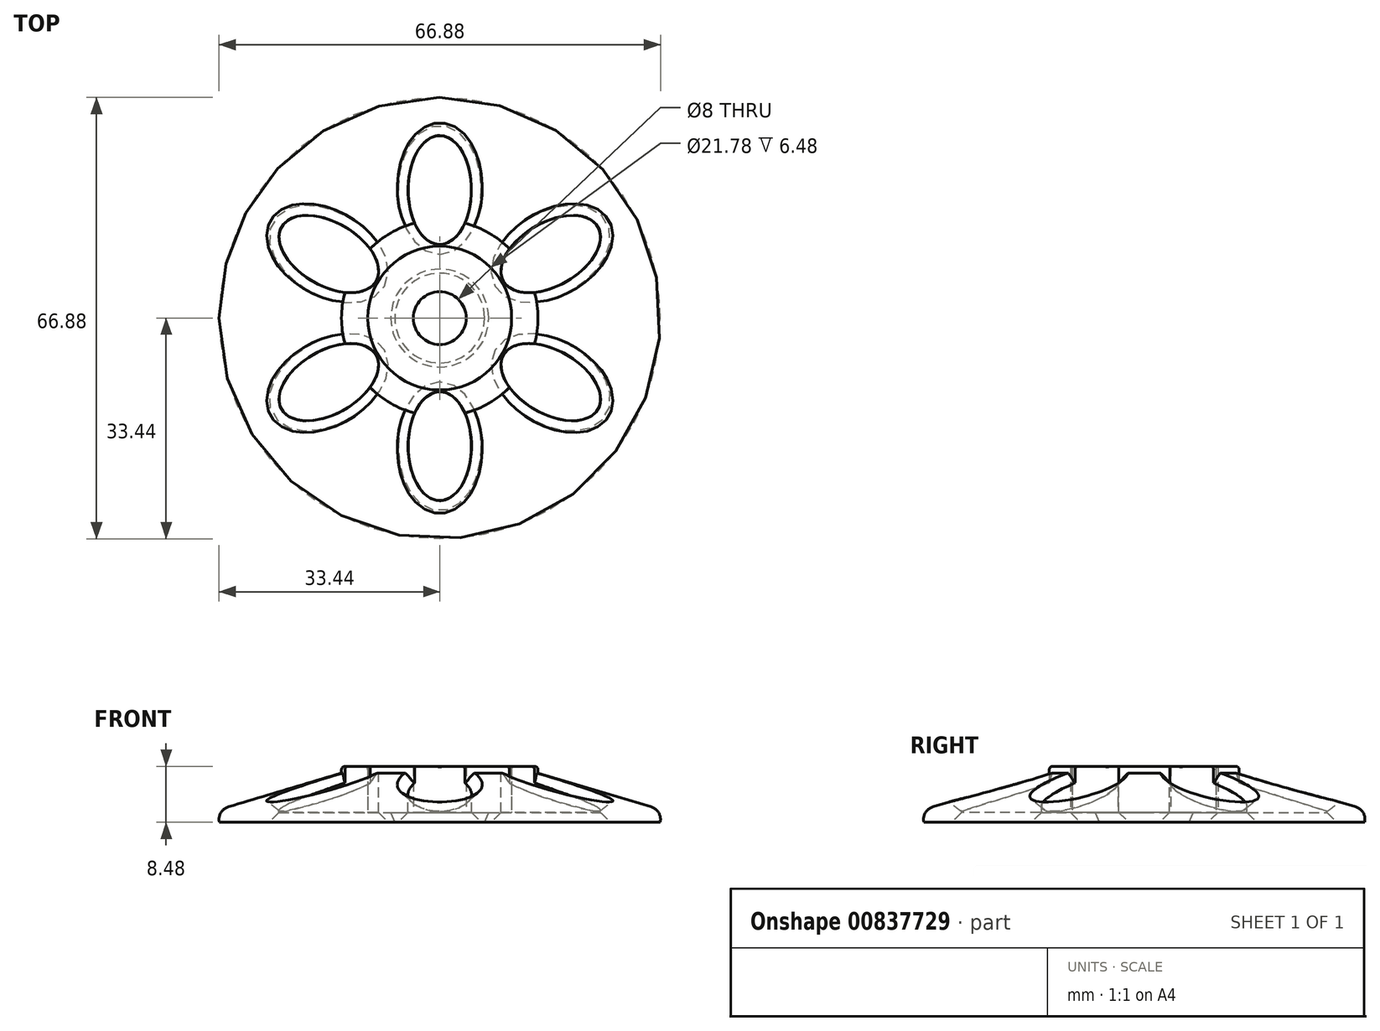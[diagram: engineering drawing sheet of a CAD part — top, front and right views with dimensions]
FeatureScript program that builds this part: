
annotation { "Feature Type Name" : "Feature", "Feature Type Description" : "" }
export const myFeature = defineFeature(function(context is Context, id is Id, definition is map)
    precondition{}
    {
        {
            var Q0;
            Q0=qCreatedBy(makeId("Front.planeOp"),FACE);
            var sketch = newSketch(context, id + "F0", { "sketchPlane" : qUnion([Q0])});
            skLineSegment(sketch, "E0", {"start": v(4, 0) * mm, "end": v(10.9, 0) * mm});
            skLineSegment(sketch, "E1", {"start": v(10.9, 0) * mm, "end": v(14.9, 0) * mm, "construction": true});
            skLineSegment(sketch, "E2.bottom", {"start": v(10.9, 0) * mm, "end": v(14.9, 0) * mm});
            skLineSegment(sketch, "E2.top", {"start": v(10.9, 6.98) * mm, "end": v(14.9, 6.98) * mm});
            skLineSegment(sketch, "E2.left", {"start": v(10.9, 0) * mm, "end": v(10.9, 6.98) * mm});
            skLineSegment(sketch, "E2.right", {"start": v(14.9, 0) * mm, "end": v(14.9, 5.98) * mm});
            skLineSegment(sketch, "E3", {"start": v(0, 0) * mm, "end": v(0, 42.81) * mm, "construction": true});
            skLineSegment(sketch, "E4", {"start": v(4, -1.5) * mm, "end": v(14.9, -1.5) * mm});
            skLineSegment(sketch, "E5", {"start": v(34.9, -1.5) * mm, "end": v(34.9, 0) * mm});
            skLineSegment(sketch, "E6", {"start": v(14.9, 0) * mm, "end": v(10.9, 0) * mm});
            skLineSegment(sketch, "E7", {"start": v(34.9, 0) * mm, "end": v(14.89, 5.98) * mm});
            skLineSegment(sketch, "E8", {"start": v(14.9, 5.98) * mm, "end": v(14.9, 6.98) * mm});
            skLineSegment(sketch, "E9", {"start": v(4, 0) * mm, "end": v(0, 0) * mm, "construction": true});
            skLineSegment(sketch, "E10", {"start": v(4, -1.5) * mm, "end": v(5, -1.5) * mm, "construction": true});
            skLineSegment(sketch, "E11", {"start": v(5, -1.5) * mm, "end": v(5, 0) * mm});
            skLineSegment(sketch, "E12.bottom", {"start": v(10.9, 0) * mm, "end": v(4, 0) * mm});
            skLineSegment(sketch, "E12.top", {"start": v(10.9, 6.98) * mm, "end": v(4, 6.98) * mm});
            skLineSegment(sketch, "E12.right", {"start": v(4, 0) * mm, "end": v(4, 6.98) * mm});
            skLineSegment(sketch, "E13", {"start": v(14.9, 0) * mm, "end": v(14.9, -1.5) * mm, "construction": true});
            skLineSegment(sketch, "E14", {"start": v(14.9, -1.5) * mm, "end": v(34.9, -1.5) * mm});
            skSolve(sketch);
        }
        {
            var Q0;
            Q0=makeQuery(id+"F0.imprint","IMPRINT",FACE,{"disambiguationData":[TD([[makeQuery(id+"F0.imprint","IMPRINT",EDGE,{"derivedFrom":sQuery(id+"F0.wireOp",EDGE,"E2.top")}),-1.0]])]});
            var Q1;
            Q1=sQuery(id+"F0.wireOp",EDGE,"E3");
            revolve(context, id + "F1", {"surfaceOperationType" : NewSurfaceOperationType.NEW, "entities" : qUnion([Q0]), "axis" : qUnion([Q1]), "revolveType" : RevolveType.FULL});
        }
        {
            var Q0;
            Q0=makeQuery(id+"F0.imprint","IMPRINT",FACE,{"disambiguationData":[TD([[makeQuery(id+"F0.imprint","IMPRINT",EDGE,{"derivedFrom":sQuery(id+"F0.wireOp",EDGE,"E12.top")}),1.0]])]});
            var Q1;
            Q1=sQuery(id+"F0.wireOp",EDGE,"E3");
            revolve(context, id + "F2", {"surfaceOperationType" : NewSurfaceOperationType.NEW, "entities" : qUnion([Q0]), "axis" : qUnion([Q1]), "revolveType" : RevolveType.FULL});
        }
        {
            var Q0;
            Q0=makeQuery(id+"F0.imprint","IMPRINT",FACE,{"disambiguationData":[TD([[makeQuery(id+"F0.imprint","IMPRINT",EDGE,{"derivedFrom":sQuery(id+"F0.wireOp",EDGE,"E2.right")}),-1.0]])]});
            var Q1;
            Q1=sQuery(id+"F0.wireOp",EDGE,"E3");
            revolve(context, id + "F3", {"surfaceOperationType" : NewSurfaceOperationType.NEW, "entities" : qUnion([Q0]), "axis" : qUnion([Q1]), "revolveType" : RevolveType.FULL});
        }
        {
            var Q0;
            Q0=qCreatedBy(makeId("Top.planeOp"),FACE);
            var sketch = newSketch(context, id + "F4", { "sketchPlane" : qUnion([Q0])});
            skPoint(sketch, "E15", {"position": v(0, 19.42) * mm});
            skEllipse(sketch, "E16", {"center": v(0, 19.42) * mm, "majorRadius": 8.25 * mm, "minorRadius": 4.8 * mm, "majorAxis": v(0, -1)});
            skSolve(sketch);
        }
        {
            var Q0;
            Q0=makeQuery(id+"F4.imprint","IMPRINT",FACE,{"disambiguationData":[TD([[makeQuery(id+"F4.imprint","IMPRINT",EDGE,{"derivedFrom":sQuery(id+"F4.wireOp",EDGE,"E16")}),1.0]])]});
            extrude(context, id + "F5", {"entities" : qUnion([Q0]), "endBound" : BoundingType.SYMMETRIC, "depth" : 25 * mm, "offsetDistance" : 25 * mm});
        }
        {
            var Q0;
            Q0=qCreatedBy(makeId("Right.planeOp"),FACE);
            var sketch = newSketch(context, id + "F6", { "sketchPlane" : qUnion([Q0])});
            skLineSegment(sketch, "E17", {"start": v(0, 0) * mm, "end": v(0, 29.58) * mm, "construction": true});
            skSolve(sketch);
        }
        {
            var Q0;
            Q0=makeQuery(id+"F5.opExtrude","SWEPT_BODY",BODY,{"disambiguationData":[OSD([sQuery(id+"F4.wireOp",EDGE,"E16")])]});
            var Q1;
            Q1=sQuery(id+"F6.wireOp",EDGE,"E17");
            circularPattern(context, id + "F7", {"operationType" : NewBodyOperationType.REMOVE, "entities" : qUnion([Q0]), "axis" : qUnion([Q1]), "angle" : 360 * degree, "instanceCount" : 6, "equalSpace" : true});
        }
        {
            var Q0;
            Q0=makeQuery(id+"F1.opRevolve","SWEPT_BODY",BODY,{"disambiguationData":[OSD([sQuery(id+"F0.wireOp",EDGE,"E2.top"),sQuery(id+"F0.wireOp",EDGE,"E2.right"),sQuery(id+"F0.wireOp",EDGE,"E6"),sQuery(id+"F0.wireOp",EDGE,"E8"),sQuery(id+"F0.wireOp",EDGE,"E2.left")])]});
            var Q1;
            Q1=makeQuery(id+"F3.opRevolve","SWEPT_BODY",BODY,{"disambiguationData":[OSD([sQuery(id+"F0.wireOp",EDGE,"E2.right"),sQuery(id+"F0.wireOp",EDGE,"E4"),sQuery(id+"F0.wireOp",EDGE,"E5"),sQuery(id+"F0.wireOp",EDGE,"E6"),sQuery(id+"F0.wireOp",EDGE,"E7"),sQuery(id+"F0.wireOp",EDGE,"E11"),sQuery(id+"F0.wireOp",EDGE,"E12.bottom"),sQuery(id+"F0.wireOp",EDGE,"E14")])]});
            booleanBodies(context, id + "F8", {"operationType" : BooleanOperationType.UNION, "tools" : qUnion([Q0, Q1])});
        }
        {
            var Q0;
            Q0=makeQuery(id+"F7.boolean.opBoolean","INTERSECT",EDGE,{"derivedFrom":[makeQuery(id+"F3.opRevolve","SWEPT_FACE",FACE,{"disambiguationData":[OSD([sQuery(id+"F0.wireOp",EDGE,"E7")])]}),makeQuery(id+"F5.opExtrude","SWEPT_FACE",FACE,{"disambiguationData":[OSD([sQuery(id+"F4.wireOp",EDGE,"E16")])]})]});
            var Q1;
            Q1=makeQuery(id+"F7.boolean.opBoolean","INTERSECT",EDGE,{"derivedFrom":[makeQuery(id+"F3.opRevolve","SWEPT_FACE",FACE,{"disambiguationData":[OSD([sQuery(id+"F0.wireOp",EDGE,"E7")])]}),makeQuery(id+"F7.opPattern","COPY",FACE,{"derivedFrom":makeQuery(id+"F5.opExtrude","SWEPT_FACE",FACE,{"disambiguationData":[OSD([sQuery(id+"F4.wireOp",EDGE,"E16")])]}),"instanceName":"5"})]});
            var Q2;
            Q2=makeQuery(id+"F7.boolean.opBoolean","INTERSECT",EDGE,{"derivedFrom":[makeQuery(id+"F3.opRevolve","SWEPT_FACE",FACE,{"disambiguationData":[OSD([sQuery(id+"F0.wireOp",EDGE,"E4")])]}),makeQuery(id+"F7.opPattern","COPY",FACE,{"derivedFrom":makeQuery(id+"F5.opExtrude","SWEPT_FACE",FACE,{"disambiguationData":[OSD([sQuery(id+"F4.wireOp",EDGE,"E16")])]}),"instanceName":"4"})]});
            var Q3;
            Q3=makeQuery(id+"F7.boolean.opBoolean","INTERSECT",EDGE,{"derivedFrom":[makeQuery(id+"F3.opRevolve","SWEPT_FACE",FACE,{"disambiguationData":[OSD([sQuery(id+"F0.wireOp",EDGE,"E7")])]}),makeQuery(id+"F7.opPattern","COPY",FACE,{"derivedFrom":makeQuery(id+"F5.opExtrude","SWEPT_FACE",FACE,{"disambiguationData":[OSD([sQuery(id+"F4.wireOp",EDGE,"E16")])]}),"instanceName":"3"})]});
            var Q4;
            Q4=makeQuery(id+"F7.boolean.opBoolean","INTERSECT",EDGE,{"derivedFrom":[makeQuery(id+"F3.opRevolve","SWEPT_FACE",FACE,{"disambiguationData":[OSD([sQuery(id+"F0.wireOp",EDGE,"E7")])]}),makeQuery(id+"F7.opPattern","COPY",FACE,{"derivedFrom":makeQuery(id+"F5.opExtrude","SWEPT_FACE",FACE,{"disambiguationData":[OSD([sQuery(id+"F4.wireOp",EDGE,"E16")])]}),"instanceName":"2"})]});
            var Q5;
            Q5=makeQuery(id+"F7.boolean.opBoolean","INTERSECT",EDGE,{"derivedFrom":[makeQuery(id+"F3.opRevolve","SWEPT_FACE",FACE,{"disambiguationData":[OSD([sQuery(id+"F0.wireOp",EDGE,"E7")])]}),makeQuery(id+"F7.opPattern","COPY",FACE,{"derivedFrom":makeQuery(id+"F5.opExtrude","SWEPT_FACE",FACE,{"disambiguationData":[OSD([sQuery(id+"F4.wireOp",EDGE,"E16")])]}),"instanceName":"1"})]});
            var Q6;
            Q6=makeQuery(id+"F7.boolean.opBoolean","INTERSECT",EDGE,{"derivedFrom":[makeQuery(id+"F3.opRevolve","SWEPT_FACE",FACE,{"disambiguationData":[OSD([sQuery(id+"F0.wireOp",EDGE,"E7")])]}),makeQuery(id+"F7.opPattern","COPY",FACE,{"derivedFrom":makeQuery(id+"F5.opExtrude","SWEPT_FACE",FACE,{"disambiguationData":[OSD([sQuery(id+"F4.wireOp",EDGE,"E16")])]}),"instanceName":"4"})]});
            var Q7;
            Q7=makeQuery(id+"F3.opRevolve","SWEPT_FACE",FACE,{"disambiguationData":[OSD([sQuery(id+"F0.wireOp",EDGE,"E4")])]});
            chamfer(context, id + "F9", {"entities" : qUnion([Q0, Q1, Q2, Q3, Q4, Q5, Q6, Q7]), "width" : 1.5 * mm, "tangentPropagation" : true});
        }
        {
            var Q0;
            Q0=makeQuery(id+"F3.opRevolve","SWEPT_EDGE",EDGE,{"disambiguationData":[OSD([sQuery(id+"F0.wireOp",EDGE,"E2.right"),sQuery(id+"F0.wireOp",EDGE,"E7")])]});
            var Q1;
            Q1=makeQuery(id+"F9.opChamfer","BLEND_EDGE",EDGE,{"blendedFrom":[makeQuery(id+"F3.opRevolve","SWEPT_EDGE",EDGE,{"disambiguationData":[OSD([sQuery(id+"F0.wireOp",EDGE,"E4"),sQuery(id+"F0.wireOp",EDGE,"scFdi4Ce-vrCE-gJmC-XL9V-FmECyV5VCvam")])]}),makeQuery(id+"F3.opRevolve","SWEPT_FACE",FACE,{"disambiguationData":[OSD([sQuery(id+"F0.wireOp",EDGE,"E0"),sQuery(id+"F0.wireOp",EDGE,"E6")])]})],"blendedInto":[makeQuery(id+"F3.opRevolve","SWEPT_FACE",FACE,{"disambiguationData":[OSD([sQuery(id+"F0.wireOp",EDGE,"E0"),sQuery(id+"F0.wireOp",EDGE,"E6")])]})]});
            chamfer(context, id + "F10", {"entities" : qUnion([Q0, Q1]), "width" : 1 * mm, "tangentPropagation" : true});
        }
        {
            var Q0;
            Q0=makeQuery(id+"F9.opChamfer","BLEND_EDGE",EDGE,{"blendedFrom":[makeQuery(id+"F3.opRevolve","SWEPT_EDGE",EDGE,{"disambiguationData":[OSD([sQuery(id+"F0.wireOp",EDGE,"E5"),sQuery(id+"F0.wireOp",EDGE,"E14")])]}),makeQuery(id+"F3.opRevolve","SWEPT_FACE",FACE,{"disambiguationData":[OSD([sQuery(id+"F0.wireOp",EDGE,"E7")])]})],"blendedInto":[makeQuery(id+"F3.opRevolve","SWEPT_FACE",FACE,{"disambiguationData":[OSD([sQuery(id+"F0.wireOp",EDGE,"E7")])]})]});
            fillet(context, id + "F11", {"entities" : qUnion([Q0]), "radius" : 2 * mm, "tangentPropagation" : true, "allowEdgeOverflow" : false});
        }
        {
            var Q0;
            Q0=makeQuery(id+"F1.opRevolve","SWEPT_EDGE",EDGE,{"disambiguationData":[OSD([sQuery(id+"F0.wireOp",EDGE,"E2.top"),sQuery(id+"F0.wireOp",EDGE,"E8")])]});
            var Q1;
            Q1=makeQuery(id+"F1.opRevolve","SWEPT_EDGE",EDGE,{"disambiguationData":[OSD([sQuery(id+"F0.wireOp",EDGE,"E2.top"),sQuery(id+"F0.wireOp",EDGE,"E12.top"),sQuery(id+"F0.wireOp",EDGE,"E2.left")])]});
            var Q2;
            {var subQ0=sQuery(id+"F0.wireOp",EDGE,"E2.right");var subQ1=sQuery(id+"F0.wireOp",EDGE,"E6");Q2=makeQuery(id+"F8.opBoolean","SPLIT",EDGE,{"disambiguationData":[TD([makeQuery(id+"F7.boolean.opBoolean","COPY",FACE,{"derivedFrom":makeQuery(id+"F7.opPattern","COPY",FACE,{"derivedFrom":makeQuery(id+"F5.opExtrude","SWEPT_FACE",FACE,{"disambiguationData":[OSD([sQuery(id+"F4.wireOp",EDGE,"E16")])]}),"instanceName":"3"})})])],"derivedFrom":makeQuery(id+"F1.opRevolve","SWEPT_EDGE",EDGE,{"disambiguationData":[OSD([subQ0,subQ1])]})});}
            var Q3;
            {var subQ0=sQuery(id+"F0.wireOp",EDGE,"E2.right");var subQ1=sQuery(id+"F0.wireOp",EDGE,"E6");Q3=makeQuery(id+"F8.opBoolean","SPLIT",EDGE,{"disambiguationData":[TD([makeQuery(id+"F7.boolean.opBoolean","COPY",FACE,{"derivedFrom":makeQuery(id+"F7.opPattern","COPY",FACE,{"derivedFrom":makeQuery(id+"F5.opExtrude","SWEPT_FACE",FACE,{"disambiguationData":[OSD([sQuery(id+"F4.wireOp",EDGE,"E16")])]}),"instanceName":"4"})})])],"derivedFrom":makeQuery(id+"F1.opRevolve","SWEPT_EDGE",EDGE,{"disambiguationData":[OSD([subQ0,subQ1])]})});}
            var Q4;
            {var subQ0=sQuery(id+"F0.wireOp",EDGE,"E2.right");var subQ1=sQuery(id+"F0.wireOp",EDGE,"E6");Q4=makeQuery(id+"F8.opBoolean","SPLIT",EDGE,{"disambiguationData":[TD([makeQuery(id+"F7.boolean.opBoolean","COPY",FACE,{"derivedFrom":makeQuery(id+"F7.opPattern","COPY",FACE,{"derivedFrom":makeQuery(id+"F5.opExtrude","SWEPT_FACE",FACE,{"disambiguationData":[OSD([sQuery(id+"F4.wireOp",EDGE,"E16")])]}),"instanceName":"2"})})])],"derivedFrom":makeQuery(id+"F1.opRevolve","SWEPT_EDGE",EDGE,{"disambiguationData":[OSD([subQ0,subQ1])]})});}
            var Q5;
            {var subQ0=sQuery(id+"F0.wireOp",EDGE,"E2.right");var subQ1=sQuery(id+"F0.wireOp",EDGE,"E6");Q5=makeQuery(id+"F8.opBoolean","SPLIT",EDGE,{"disambiguationData":[TD([makeQuery(id+"F7.boolean.opBoolean","COPY",FACE,{"derivedFrom":makeQuery(id+"F7.opPattern","COPY",FACE,{"derivedFrom":makeQuery(id+"F5.opExtrude","SWEPT_FACE",FACE,{"disambiguationData":[OSD([sQuery(id+"F4.wireOp",EDGE,"E16")])]}),"instanceName":"1"})})])],"derivedFrom":makeQuery(id+"F1.opRevolve","SWEPT_EDGE",EDGE,{"disambiguationData":[OSD([subQ0,subQ1])]})});}
            var Q6;
            {var subQ0=sQuery(id+"F0.wireOp",EDGE,"E2.right");var subQ1=sQuery(id+"F0.wireOp",EDGE,"E6");Q6=makeQuery(id+"F8.opBoolean","SPLIT",EDGE,{"disambiguationData":[TD([makeQuery(id+"F7.boolean.opBoolean","COPY",FACE,{"derivedFrom":makeQuery(id+"F5.opExtrude","SWEPT_FACE",FACE,{"disambiguationData":[OSD([sQuery(id+"F4.wireOp",EDGE,"E16")])]})})])],"derivedFrom":makeQuery(id+"F1.opRevolve","SWEPT_EDGE",EDGE,{"disambiguationData":[OSD([subQ0,subQ1])]})});}
            var Q7;
            {var subQ0=sQuery(id+"F0.wireOp",EDGE,"E2.right");var subQ1=sQuery(id+"F0.wireOp",EDGE,"E6");Q7=makeQuery(id+"F8.opBoolean","SPLIT",EDGE,{"disambiguationData":[TD([makeQuery(id+"F7.boolean.opBoolean","COPY",FACE,{"derivedFrom":makeQuery(id+"F7.opPattern","COPY",FACE,{"derivedFrom":makeQuery(id+"F5.opExtrude","SWEPT_FACE",FACE,{"disambiguationData":[OSD([sQuery(id+"F4.wireOp",EDGE,"E16")])]}),"instanceName":"5"})})])],"derivedFrom":makeQuery(id+"F1.opRevolve","SWEPT_EDGE",EDGE,{"disambiguationData":[OSD([subQ0,subQ1])]})});}
            var Q8;
            {var subQ0=sQuery(id+"F0.wireOp",EDGE,"E4");Q8=makeQuery(id+"F10.opChamfer","BLEND_EDGE",EDGE,{"blendedFrom":[makeQuery(id+"F9.opChamfer","BLEND_EDGE",EDGE,{"blendedFrom":[makeQuery(id+"F3.opRevolve","SWEPT_EDGE",EDGE,{"disambiguationData":[OSD([subQ0,sQuery(id+"F0.wireOp",EDGE,"E11")])]}),makeQuery(id+"F3.opRevolve","SWEPT_FACE",FACE,{"disambiguationData":[OSD([sQuery(id+"F0.wireOp",EDGE,"E6"),sQuery(id+"F0.wireOp",EDGE,"E12.bottom")])]})],"blendedInto":[makeQuery(id+"F3.opRevolve","SWEPT_FACE",FACE,{"disambiguationData":[OSD([sQuery(id+"F0.wireOp",EDGE,"E6"),sQuery(id+"F0.wireOp",EDGE,"E12.bottom")])]})]}),makeQuery(id+"F3.opRevolve","SWEPT_FACE",FACE,{"disambiguationData":[OSD([subQ0,sQuery(id+"F0.wireOp",EDGE,"E14")])]})],"blendedInto":[makeQuery(id+"F3.opRevolve","SWEPT_FACE",FACE,{"disambiguationData":[OSD([subQ0,sQuery(id+"F0.wireOp",EDGE,"E14")])]})]});}
            fillet(context, id + "F12", {"entities" : qUnion([Q0, Q1, Q2, Q3, Q4, Q5, Q6, Q7, Q8]), "radius" : 0.5 * mm, "tangentPropagation" : true, "allowEdgeOverflow" : false});
        }
    });
